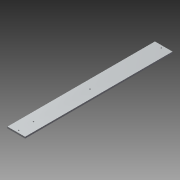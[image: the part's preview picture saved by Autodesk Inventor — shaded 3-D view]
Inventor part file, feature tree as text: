
AUTODESK INVENTOR PART (.ipt)
format: ipt  version: 2015 SP1 (Build 190203100, 203)  size: 94,720 bytes
history: native  units: mm
features: reference x3, sketch x2, extrude x1, hole x1
ambient origin geometry x8: Origin, YZ Plane, XZ Plane, XY Plane, X Axis, Y Axis, Z Axis, Center Point
bodies: Solid1 (feature_tree)
feature tree (7):
  extrude  "Extrusion1"  Depth=6.35mm
  hole  "Hole1"  [1 undecoded]
  sketch  "Sketch1"  dims[d0=6.35mm d1=0.0mm d2=20.0mm]
  reference  "Reference1"
  reference  "Reference2"
  reference  "Reference4"
  sketch  "Sketch2"  dims[d3=140.0mm d4=20.0mm d5=4.5mm d6=6.0mm d7=8.0mm d8=4.0mm d9=90.0deg d10=8.0mm d11=20.594885mm]
note: 1 required parameter value undecoded (feature->parameter linkage not recoverable at this tier; creation-order binding heuristic only, values carry confidence <= 0.55)
